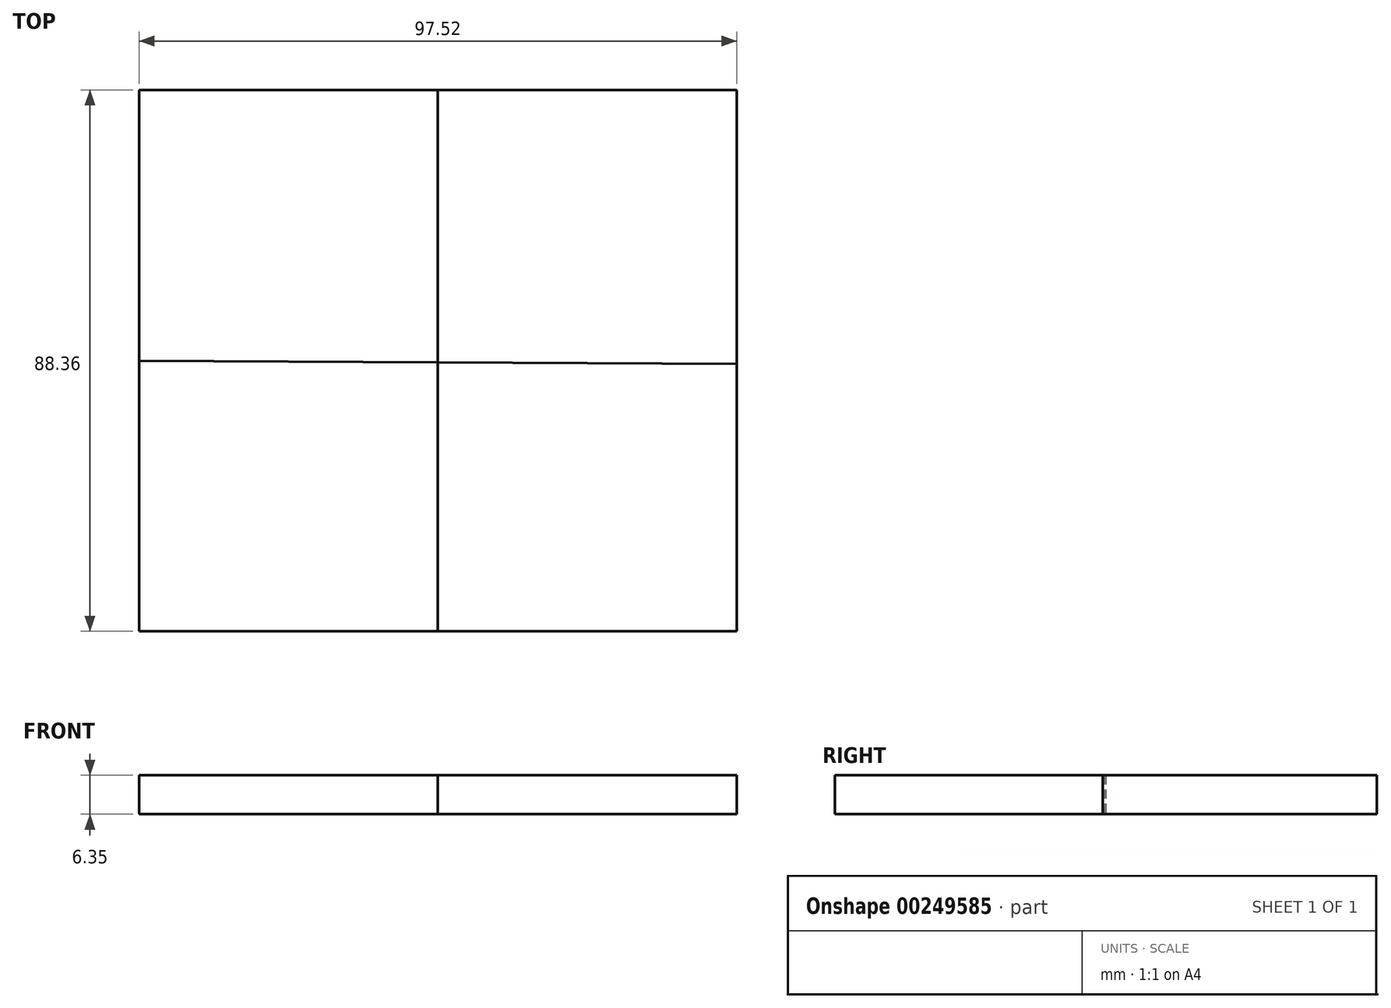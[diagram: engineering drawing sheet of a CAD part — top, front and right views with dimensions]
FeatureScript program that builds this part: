
annotation { "Feature Type Name" : "Feature", "Feature Type Description" : "" }
export const myFeature = defineFeature(function(context is Context, id is Id, definition is map)
    precondition{}
    {
        {
            var Q0;
            Q0=qCreatedBy(makeId("Top.planeOp"),FACE);
            var sketch = newSketch(context, id + "F0", { "sketchPlane" : qUnion([Q0])});
            skLineSegment(sketch, "E0.bottom", {"start": v(-47.95, 44.72) * mm, "end": v(49.57, 44.72) * mm});
            skLineSegment(sketch, "E0.top", {"start": v(-47.95, -43.64) * mm, "end": v(49.57, -43.64) * mm});
            skLineSegment(sketch, "E0.left", {"start": v(-47.95, 44.72) * mm, "end": v(-47.95, -43.64) * mm});
            skLineSegment(sketch, "E0.right", {"start": v(49.57, 44.72) * mm, "end": v(49.57, -43.64) * mm});
            skLineSegment(sketch, "E1", {"start": v(0.8, 44.72) * mm, "end": v(0.8, -43.64) * mm});
            skLineSegment(sketch, "E2", {"start": v(-47.95, 0.54) * mm, "end": v(49.57, 0) * mm});
            skSolve(sketch);
        }
        {
            var Q0;
            {var subQ0=sQuery(id+"F0.wireOp",EDGE,"E0.left");var subQ1=sQuery(id+"F0.wireOp",EDGE,"E0.bottom");var subQ2=makeQuery(id+"F0.imprint","INTERSECT",VERTEX,{"derivedFrom":[subQ1,subQ0]});Q0=makeQuery(id+"F0.imprint","IMPRINT",FACE,{"disambiguationData":[TD([[makeQuery(id+"F0.imprint","IMPRINT",EDGE,{"disambiguationData":[TD([[subQ2,-1.0]])],"derivedFrom":subQ1}),-1.0]])]});}
            var Q1;
            {var subQ0=sQuery(id+"F0.wireOp",EDGE,"E0.right");var subQ1=sQuery(id+"F0.wireOp",EDGE,"E0.top");var subQ2=makeQuery(id+"F0.imprint","INTERSECT",VERTEX,{"derivedFrom":[subQ1,subQ0]});Q1=makeQuery(id+"F0.imprint","IMPRINT",FACE,{"disambiguationData":[TD([[makeQuery(id+"F0.imprint","IMPRINT",EDGE,{"disambiguationData":[TD([[subQ2,1.0]])],"derivedFrom":subQ1}),1.0]])]});}
            extrude(context, id + "F1", {"entities" : qUnion([Q0, Q1]), "depth" : 6.35 * mm});
        }
        {
            var Q0;
            {var subQ0=sQuery(id+"F0.wireOp",EDGE,"E0.left");var subQ1=sQuery(id+"F0.wireOp",EDGE,"E0.top");var subQ2=makeQuery(id+"F0.imprint","INTERSECT",VERTEX,{"derivedFrom":[subQ1,subQ0]});Q0=makeQuery(id+"F0.imprint","IMPRINT",FACE,{"disambiguationData":[TD([[makeQuery(id+"F0.imprint","IMPRINT",EDGE,{"disambiguationData":[TD([[subQ2,-1.0]])],"derivedFrom":subQ1}),1.0]])]});}
            var Q1;
            {var subQ0=sQuery(id+"F0.wireOp",EDGE,"E0.right");var subQ1=sQuery(id+"F0.wireOp",EDGE,"E0.bottom");var subQ2=makeQuery(id+"F0.imprint","INTERSECT",VERTEX,{"derivedFrom":[subQ1,subQ0]});Q1=makeQuery(id+"F0.imprint","IMPRINT",FACE,{"disambiguationData":[TD([[makeQuery(id+"F0.imprint","IMPRINT",EDGE,{"disambiguationData":[TD([[subQ2,1.0]])],"derivedFrom":subQ1}),-1.0]])]});}
            extrude(context, id + "F2", {"entities" : qUnion([Q0, Q1]), "depth" : 6.35 * mm});
        }
    });
